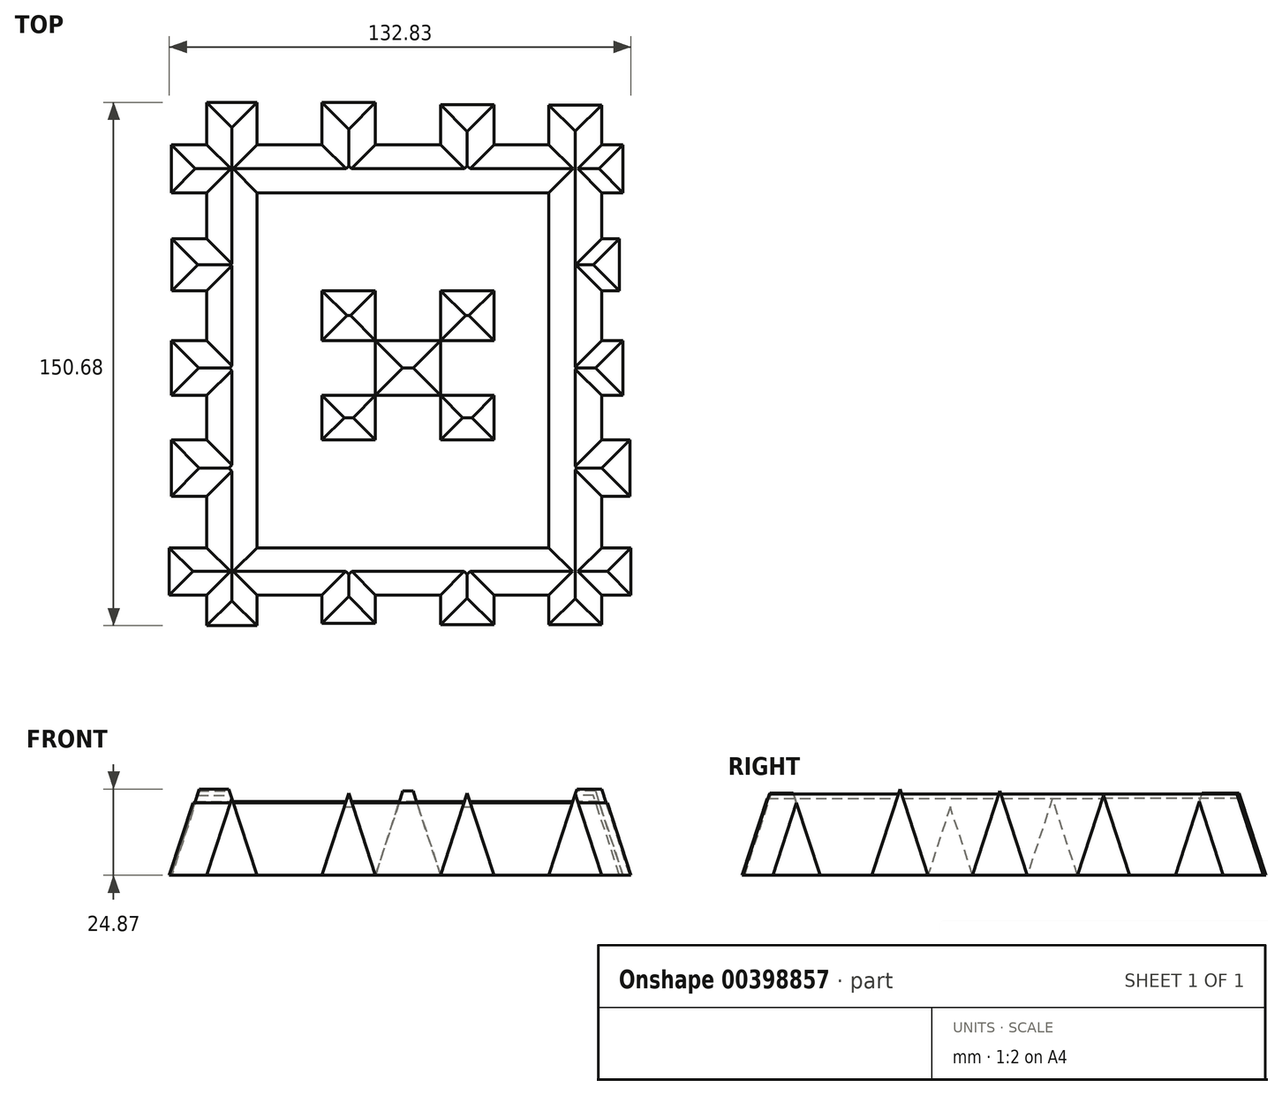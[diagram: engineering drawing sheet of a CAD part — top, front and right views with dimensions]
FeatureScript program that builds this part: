
annotation { "Feature Type Name" : "Feature", "Feature Type Description" : "" }
export const myFeature = defineFeature(function(context is Context, id is Id, definition is map)
    precondition{}
    {
        {
            var Q0;
            Q0=qCreatedBy(makeId("Top.planeOp"),FACE);
            var sketch = newSketch(context, id + "F0", { "sketchPlane" : qUnion([Q0])});
            skLineSegment(sketch, "E0.bottom", {"start": v(-64.64, -53.8) * mm, "end": v(68.19, -53.8) * mm});
            skLineSegment(sketch, "E0.top", {"start": v(-64.64, -67.4) * mm, "end": v(68.19, -67.4) * mm});
            skLineSegment(sketch, "E0.left", {"start": v(-64.64, -53.8) * mm, "end": v(-64.64, -67.4) * mm});
            skLineSegment(sketch, "E0.right", {"start": v(68.19, -53.8) * mm, "end": v(68.19, -67.4) * mm});
            skLineSegment(sketch, "E1.bottom", {"start": v(-64.08, -22.77) * mm, "end": v(67.85, -22.77) * mm});
            skLineSegment(sketch, "E1.top", {"start": v(-64.08, -38.93) * mm, "end": v(67.85, -38.93) * mm});
            skLineSegment(sketch, "E1.left", {"start": v(-64.08, -22.77) * mm, "end": v(-64.08, -38.93) * mm});
            skLineSegment(sketch, "E1.right", {"start": v(67.85, -22.77) * mm, "end": v(67.85, -38.93) * mm});
            skLineSegment(sketch, "E2.bottom", {"start": v(-64.08, 5.82) * mm, "end": v(65.88, 5.82) * mm});
            skLineSegment(sketch, "E2.top", {"start": v(-64.08, -9.94) * mm, "end": v(65.88, -9.94) * mm});
            skLineSegment(sketch, "E2.left", {"start": v(-64.08, 5.82) * mm, "end": v(-64.08, -9.94) * mm});
            skLineSegment(sketch, "E2.right", {"start": v(65.88, 5.82) * mm, "end": v(65.88, -9.94) * mm});
            skLineSegment(sketch, "E3.bottom", {"start": v(-63.89, 35.2) * mm, "end": v(64.89, 35.2) * mm});
            skLineSegment(sketch, "E3.top", {"start": v(-63.89, 20.23) * mm, "end": v(64.89, 20.23) * mm});
            skLineSegment(sketch, "E3.left", {"start": v(-63.89, 35.2) * mm, "end": v(-63.89, 20.23) * mm});
            skLineSegment(sketch, "E3.right", {"start": v(64.89, 35.2) * mm, "end": v(64.89, 20.23) * mm});
            skLineSegment(sketch, "E4.bottom", {"start": v(-64.08, 62.22) * mm, "end": v(65.88, 62.22) * mm});
            skLineSegment(sketch, "E4.top", {"start": v(-64.08, 48.43) * mm, "end": v(65.88, 48.43) * mm});
            skLineSegment(sketch, "E4.left", {"start": v(-64.08, 62.22) * mm, "end": v(-64.08, 48.43) * mm});
            skLineSegment(sketch, "E4.right", {"start": v(65.88, 62.22) * mm, "end": v(65.88, 48.43) * mm});
            skLineSegment(sketch, "E5.bottom", {"start": v(-53.83, 74.43) * mm, "end": v(-39.43, 74.43) * mm});
            skLineSegment(sketch, "E5.top", {"start": v(-53.83, -76.25) * mm, "end": v(-39.43, -76.25) * mm});
            skLineSegment(sketch, "E5.left", {"start": v(-53.83, 74.43) * mm, "end": v(-53.83, -76.25) * mm});
            skLineSegment(sketch, "E5.right", {"start": v(-39.43, 74.43) * mm, "end": v(-39.43, -76.25) * mm});
            skLineSegment(sketch, "E6.bottom", {"start": v(-20.7, 74.39) * mm, "end": v(-5.32, 74.39) * mm});
            skLineSegment(sketch, "E6.top", {"start": v(-20.7, -75.51) * mm, "end": v(-5.32, -75.51) * mm});
            skLineSegment(sketch, "E6.left", {"start": v(-20.7, 74.39) * mm, "end": v(-20.7, -75.51) * mm});
            skLineSegment(sketch, "E6.right", {"start": v(-5.32, 74.39) * mm, "end": v(-5.32, -75.51) * mm});
            skLineSegment(sketch, "E7.bottom", {"start": v(13.42, 73.75) * mm, "end": v(28.8, 73.75) * mm});
            skLineSegment(sketch, "E7.top", {"start": v(13.42, -75.95) * mm, "end": v(28.8, -75.95) * mm});
            skLineSegment(sketch, "E7.left", {"start": v(13.42, 73.75) * mm, "end": v(13.42, -75.95) * mm});
            skLineSegment(sketch, "E7.right", {"start": v(28.8, 73.75) * mm, "end": v(28.8, -75.95) * mm});
            skLineSegment(sketch, "E8.bottom", {"start": v(44.58, 73.7) * mm, "end": v(59.76, 73.7) * mm});
            skLineSegment(sketch, "E8.top", {"start": v(44.58, -76) * mm, "end": v(59.76, -76) * mm});
            skLineSegment(sketch, "E8.left", {"start": v(44.58, 73.7) * mm, "end": v(44.58, -76) * mm});
            skLineSegment(sketch, "E8.right", {"start": v(59.76, 73.7) * mm, "end": v(59.76, -76) * mm});
            skSolve(sketch);
        }
        {
            var Q0;
            Q0 = qSketchRegion(id + "F0", true);
            extrude(context, id + "F1", {"entities" : qUnion([Q0]), "depth" : 25.4 * mm, "hasDraft" : true, "draftAngle" : 18 * degree, "draftPullDirection" : true});
        }
        {
            var Q0;
            {var subQ0=sQuery(id+"F0.wireOp",EDGE,"E6.left");var subQ1=sQuery(id+"F0.wireOp",EDGE,"E2.bottom");var subQ2=makeQuery(id+"F0.imprint","INTERSECT",VERTEX,{"derivedFrom":[subQ1,subQ0]});Q0=makeQuery(id+"F0.imprint","IMPRINT",FACE,{"disambiguationData":[TD([[makeQuery(id+"F0.imprint","IMPRINT",EDGE,{"disambiguationData":[TD([[subQ2,-1.0]])],"derivedFrom":subQ1}),1.0]])]});}
            var Q1;
            {var subQ0=sQuery(id+"F0.wireOp",EDGE,"E7.left");var subQ1=sQuery(id+"F0.wireOp",EDGE,"E2.bottom");var subQ2=makeQuery(id+"F0.imprint","INTERSECT",VERTEX,{"derivedFrom":[subQ1,subQ0]});Q1=makeQuery(id+"F0.imprint","IMPRINT",FACE,{"disambiguationData":[TD([[makeQuery(id+"F0.imprint","IMPRINT",EDGE,{"disambiguationData":[TD([[subQ2,-1.0]])],"derivedFrom":subQ1}),1.0]])]});}
            var Q2;
            {var subQ0=sQuery(id+"F0.wireOp",EDGE,"E6.left");var subQ1=sQuery(id+"F0.wireOp",EDGE,"E1.bottom");var subQ2=makeQuery(id+"F0.imprint","INTERSECT",VERTEX,{"derivedFrom":[subQ1,subQ0]});Q2=makeQuery(id+"F0.imprint","IMPRINT",FACE,{"disambiguationData":[TD([[makeQuery(id+"F0.imprint","IMPRINT",EDGE,{"disambiguationData":[TD([[subQ2,-1.0]])],"derivedFrom":subQ1}),1.0]])]});}
            var Q3;
            {var subQ0=sQuery(id+"F0.wireOp",EDGE,"E6.right");var subQ1=sQuery(id+"F0.wireOp",EDGE,"E2.bottom");var subQ2=makeQuery(id+"F0.imprint","INTERSECT",VERTEX,{"derivedFrom":[subQ1,subQ0]});Q3=makeQuery(id+"F0.imprint","IMPRINT",FACE,{"disambiguationData":[TD([[makeQuery(id+"F0.imprint","IMPRINT",EDGE,{"disambiguationData":[TD([[subQ2,-1.0]])],"derivedFrom":subQ1}),-1.0]])]});}
            var Q4;
            {var subQ0=sQuery(id+"F0.wireOp",EDGE,"E7.left");var subQ1=sQuery(id+"F0.wireOp",EDGE,"E1.bottom");var subQ2=makeQuery(id+"F0.imprint","INTERSECT",VERTEX,{"derivedFrom":[subQ1,subQ0]});Q4=makeQuery(id+"F0.imprint","IMPRINT",FACE,{"disambiguationData":[TD([[makeQuery(id+"F0.imprint","IMPRINT",EDGE,{"disambiguationData":[TD([[subQ2,-1.0]])],"derivedFrom":subQ1}),1.0]])]});}
            extrude(context, id + "F2", {"entities" : qUnion([Q0, Q1, Q2, Q3, Q4]), "depth" : 254 * mm, "hasDraft" : true, "draftAngle" : 18 * degree, "draftPullDirection" : true});
        }
    });
